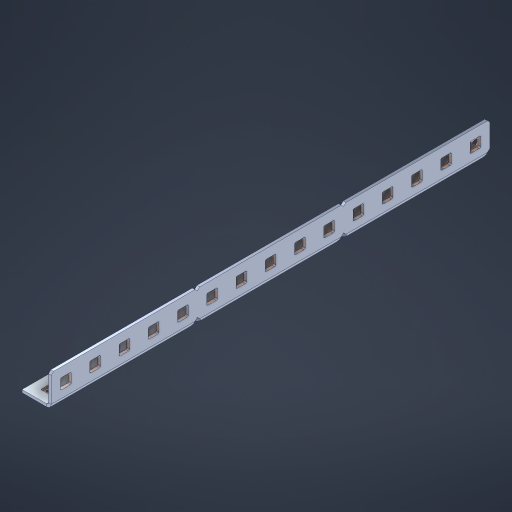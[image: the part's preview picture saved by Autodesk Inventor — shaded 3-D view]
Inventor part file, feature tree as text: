
AUTODESK INVENTOR PART (.ipt)
format: ipt  version: 2023 (Build 270158000, 158)  size: 652,800 bytes
history: native  units: in
note: dims shown in document units (in); Inventor stores cm internally (conversion verified against a paired STEP export)
features: other x35, extrude x29, sheet_metal_op x10, sketch x8, mirror x1, pattern_linear x1, chamfer x1
ambient origin geometry x8: Origin, YZ Plane, XZ Plane, XY Plane, X Axis, Y Axis, Z Axis, Center Point
bodies: Solid1 (feature_tree), Body (feature_tree)
feature tree (85):
  other  "Flange Pattern Plane"
  sheet_metal_op  "Flange Pattern"
  sheet_metal_op  "Body Pattern"
  other  "Arc Length"
  mirror  "Notch Mirror"
  pattern_linear  "Notch Pattern"  Spacing1=0.1875in  [1 undecoded]
  chamfer  "End Chamfer"
  extrude  "Half Cut"  Depth=0.0469in
  sketch  "Sketch1"  dims[d0=2.5in]
  other  "Plate1"
  sketch  "Sketch2"  dims[d1=7.5in]
  other  "Plate2"
  sheet_metal_op  "Bend1"
  sheet_metal_op  "Corner1"
  sketch  "Sketch3"  dims[d2=0.0469in]
  other  "Flange Pattern Sketch"
  sketch  "Sketch7"  dims[d3=0.0469in]
  other  "Srf1"
  other  "Srf2"
  sketch  "Sketch8"  dims[d4=0.0234in]
  sketch  "Sketch9"  dims[d5=0.0938in]
  other  "Srf91"
  sheet_metal_op  "Body Pattern Sketch"
  other  "Srf92"
  sketch  "Sketch13"  dims[d6=0.0469in]
  sketch  "Sketch14"  dims[d7=0.5in d8=90.0deg d9=0.0312in d10=0.1875in d11=0.0469in d12=0.0469in d16=0.182in d17=0.02in d18=0.0469in d19=0.0in d20=0.25in d21=0.25in d46=0.172in d47=1.0in d48=0.0in d49=0.182in d50=0.02in d51=0.25in d52=0.25in d53=0.0469in d54=0.0in d55=0.172in d56=1.0in d57=0.0in d60=5.9055in d62=0.5in d63=0.3937in d65=0.5in d85=0.1227in d86=0.1659in d88=0.04in d89=0.0469in d90=0.0in d91=0.04in d92=0.0491in d95=2.5in d96=0.04in d97=0.25in d98=45.0deg d101=0.0in d102=2.497in d131=0.5in d132=5.9055in d134=0.5in d139=0.5in]
  other  "Srf856"
  other  "Srf1310"
  other  "Srf1311"
  other  "Srf1312"
  other  "Srf1376"
  other  "Srf1377"
  other  "Srf1728"
  other  "Srf1755"
  other  "Srf1878"
  other  "Srf1879"
  other  "Srf1880"
  other  "Srf1881"
  other  "Srf1882"
  other  "Srf1883"
  other  "Srf1884"
  other  "Srf1885"
  other  "Srf1886"
  other  "Srf1942"
  other  "Srf1943"
  other  "Srf1944"
  other  "Srf1945"
  other  "Srf1946"
  other  "Srf1947"
  other  "Srf1948"
  other  "Srf1949"
  other  "Srf1950"
  sheet_metal_op  "Flange Stamp"
  sheet_metal_op  "Flange Circle"
  sheet_metal_op  "Body Stamp"
  sheet_metal_op  "Body Circle"
  sheet_metal_op  "Notch"
  extrude  "ExtrusionSrf2"  Depth=0.0469in
  extrude  "ExtrusionSrf92"  Depth=0.5in
  extrude  "ExtrusionSrf856"  Depth=0.02in
  extrude  "ExtrusionSrf1310"  Depth=0.0469in
  extrude  "ExtrusionSrf1311"  TaperAngle=0.0deg  [1 undecoded]
  extrude  "ExtrusionSrf1312"  Depth=0.5in
  extrude  "ExtrusionSrf1376"  Depth=0.5in
  extrude  "ExtrusionSrf1377"  Depth=0.5in
  extrude  "ExtrusionSrf1728"  Depth=0.5in TaperAngle=0.0deg
  extrude  "ExtrusionSrf1755"  Depth=0.5in
  extrude  "ExtrusionSrf1878"  Depth=0.02in
  extrude  "ExtrusionSrf1879"  Depth=0.5in
  extrude  "ExtrusionSrf1880"  Depth=0.5in
  extrude  "ExtrusionSrf1881"  Depth=0.0469in
  extrude  "ExtrusionSrf1882"  TaperAngle=0.0deg  [1 undecoded]
  extrude  "ExtrusionSrf1883"  Depth=0.5in
  extrude  "ExtrusionSrf1884"  Depth=0.5in TaperAngle=0.0deg
  extrude  "ExtrusionSrf1885"  Depth=0.5in
  extrude  "ExtrusionSrf1886"  Depth=0.5in
  extrude  "ExtrusionSrf1942"  Depth=0.5in
  extrude  "ExtrusionSrf1943"  Depth=0.5in
  extrude  "ExtrusionSrf1944"  Depth=0.5in
  extrude  "ExtrusionSrf1945"  Depth=0.0469in
  extrude  "ExtrusionSrf1946"  TaperAngle=0.0deg  [1 undecoded]
  extrude  "ExtrusionSrf1947"  Depth=0.5in
  extrude  "ExtrusionSrf1948"  Depth=0.5in
  extrude  "ExtrusionSrf1949"  Depth=0.5in
  extrude  "ExtrusionSrf1950"  Depth=0.5in TaperAngle=45.0deg
note: 4 required parameter values undecoded (feature->parameter linkage not recoverable at this tier; creation-order binding heuristic only, values carry confidence <= 0.55)
